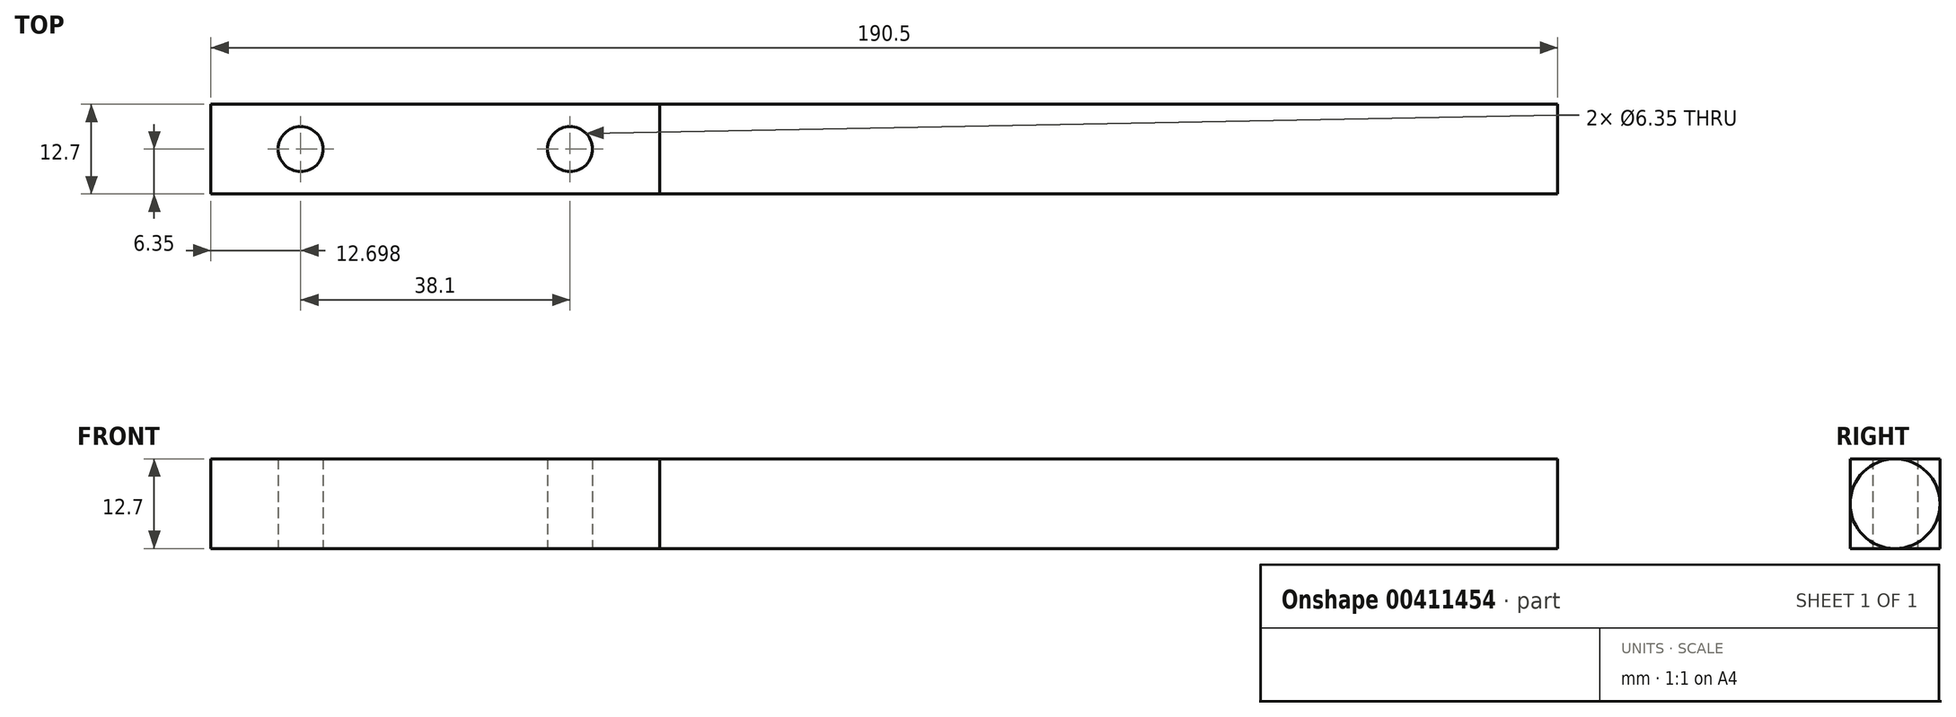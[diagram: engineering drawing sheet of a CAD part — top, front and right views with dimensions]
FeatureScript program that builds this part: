
annotation { "Feature Type Name" : "Feature", "Feature Type Description" : "" }
export const myFeature = defineFeature(function(context is Context, id is Id, definition is map)
    precondition{}
    {
        {
            var Q0;
            Q0=qCreatedBy(makeId("Top.planeOp"),FACE);
            var sketch = newSketch(context, id + "F0", { "sketchPlane" : qUnion([Q0])});
            skLineSegment(sketch, "E0.bottom", {"start": v(-27.13, 6.35) * mm, "end": v(36.37, 6.35) * mm});
            skLineSegment(sketch, "E0.top", {"start": v(-27.13, -6.35) * mm, "end": v(36.37, -6.35) * mm});
            skLineSegment(sketch, "E0.left", {"start": v(-27.13, 6.35) * mm, "end": v(-27.13, -6.35) * mm});
            skLineSegment(sketch, "E0.right", {"start": v(36.37, 6.35) * mm, "end": v(36.37, -6.35) * mm});
            skCircle(sketch, "E1", {"center": v(-14.43, 0) * mm, "radius": 3.18 * mm});
            skCircle(sketch, "E2", {"center": v(23.67, 0) * mm, "radius": 3.18 * mm});
            skSolve(sketch);
        }
        {
            var Q0;
            Q0=makeQuery(id+"F0.imprint","IMPRINT",FACE,{"disambiguationData":[TD([[makeQuery(id+"F0.imprint","IMPRINT",EDGE,{"derivedFrom":sQuery(id+"F0.wireOp",EDGE,"E0.bottom")}),-1.0]])]});
            extrude(context, id + "F1", {"entities" : qUnion([Q0]), "depth" : 12.7 * mm});
        }
        {
            var Q0;
            Q0=makeQuery(id+"F1.opExtrude","SWEPT_FACE",FACE,{"disambiguationData":[OSD([sQuery(id+"F0.wireOp",EDGE,"E0.right")])]});
            var sketch = newSketch(context, id + "F2", { "sketchPlane" : qUnion([Q0])});
            skCircle(sketch, "E3", {"center": v(0, 6.35) * mm, "radius": 6.35 * mm});
            skSolve(sketch);
        }
        {
            var Q0;
            {var subQ0=sQuery(id+"F2.wireOp",EDGE,"E3");var subQ1=sQuery(id+"F0.wireOp",EDGE,"E0.right");var subQ2=makeQuery(id+"F2.imprint","INTERSECT",VERTEX,{"derivedFrom":[makeQuery(id+"F1.opExtrude","CAP_EDGE",EDGE,{"disambiguationData":[OSD([subQ1])],"isStart":false}),subQ0]});Q0=makeQuery(id+"F2.imprint","IMPRINT",FACE,{"disambiguationData":[TD([[makeQuery(id+"F2.imprint","IMPRINT",EDGE,{"disambiguationData":[TD([[subQ2,1.0]])],"derivedFrom":subQ0}),1.0]])]});}
            extrude(context, id + "F3", {"entities" : qUnion([Q0]), "operationType" : NewBodyOperationType.ADD, "depth" : 127 * mm});
        }
    });
